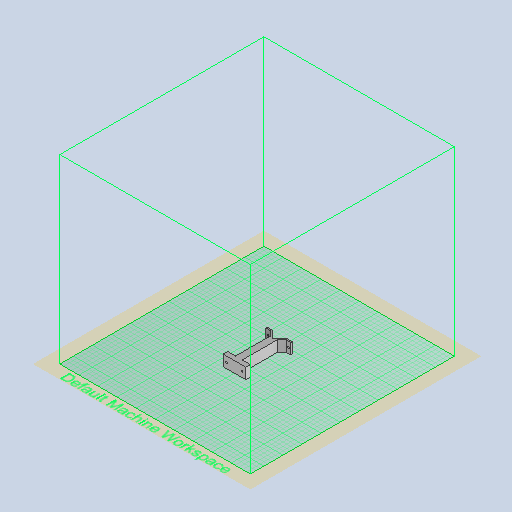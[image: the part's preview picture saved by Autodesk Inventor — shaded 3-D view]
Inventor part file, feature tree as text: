
AUTODESK INVENTOR PART (.ipt)
format: ipt  version: 2022 (Build 260153000, 153)  size: 318,976 bytes
history: native  units: mm
features: sketch x3, hole x2, extrude x1, chamfer x1
ambient origin geometry x8: Origin, YZ Plane, XZ Plane, XY Plane, X Axis, Y Axis, Z Axis, Center Point
bodies: Body1 (feature_tree)
feature tree (7):
  extrude  "Extrusion3"  TaperAngle=45.0deg  [1 undecoded]
  hole  "Hole2"  [1 undecoded]
  chamfer  "Chamfer2"  Angle=45.0deg  [1 undecoded]
  hole  "Hole3"  [1 undecoded]
  sketch  "Sketch1"  dims[d34=23.0mm d35=45.0deg]
  sketch  "Sketch4"  dims[d36=23.0mm d37=3.0mm]
  sketch  "Sketch5"  dims[d38=3.0mm d39=45.0deg d41=6.0mm d49=10.0mm d50=6.0mm d51=3.0mm d52=10.0mm d69=15.0mm d70=50.0mm d71=10.0mm d72=100.0mm d73=24.0mm d74=0.0mm d75=12.0mm d76=12.0mm d77=5.0mm d78=5.0mm d79=4.0mm d80=6.0mm d81=4.0mm d82=2.0mm d83=90.0deg d84=8.0mm d85=20.594885mm d86=2.0mm d87=2.0mm d88=45.0deg d91=12.0mm d92=12.0mm d93=8.0mm d94=8.0mm d95=4.0mm d96=6.0mm d97=4.0mm d98=2.0mm d99=90.0deg d100=8.0mm d101=20.594885mm]
note: 4 required parameter values undecoded (feature->parameter linkage not recoverable at this tier; creation-order binding heuristic only, values carry confidence <= 0.55)
